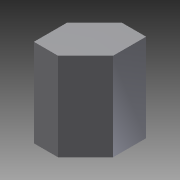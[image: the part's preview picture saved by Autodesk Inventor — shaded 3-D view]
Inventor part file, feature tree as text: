
AUTODESK INVENTOR PART (.ipt)
format: ipt  version: 2012 SP2 (Build 160219200, 219)  size: 83,968 bytes
history: native  units: in
note: dims shown in document units (in); Inventor stores cm internally (conversion verified against a paired STEP export)
features: extrude x2, chamfer x2, sketch x2
ambient origin geometry x8: Origin, YZ Plane, XZ Plane, XY Plane, X Axis, Y Axis, Z Axis, Center Point
bodies: Solid1 (feature_tree)
feature tree (6):
  extrude  "Extrusion1"  Depth=1.25in TaperAngle=45.0deg
  chamfer  "Chamfer1"  Distance=1.25in Angle=45.0deg
  chamfer  "Chamfer2"  Distance=1.8125in
  extrude  "Extrusion2"  [1 undecoded]
  sketch  "Sketch1"  dims[d0=1.8125in d1=0.938in d2=0.0in d3=0.0in d4=1.25in d5=0.125in d6=45.0deg d7=1.25in d8=0.125in d9=45.0deg]
  sketch  "Sketch2"  dims[d11=0.7874in d12=1.8125in d13=0.0in]
note: 1 required parameter value undecoded (feature->parameter linkage not recoverable at this tier; creation-order binding heuristic only, values carry confidence <= 0.55)
